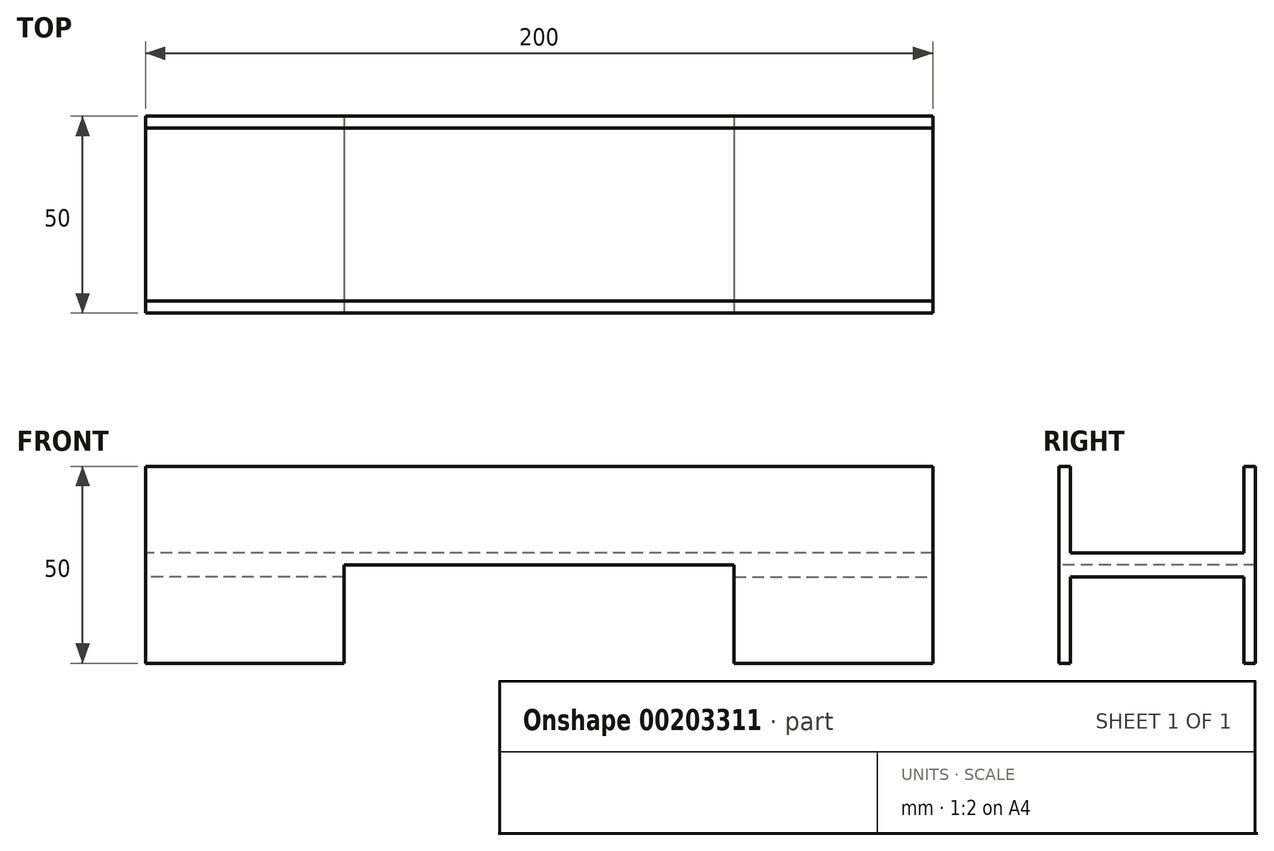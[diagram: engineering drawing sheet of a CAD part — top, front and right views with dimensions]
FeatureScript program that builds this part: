
annotation { "Feature Type Name" : "Feature", "Feature Type Description" : "" }
export const myFeature = defineFeature(function(context is Context, id is Id, definition is map)
    precondition{}
    {
        {
            var Q0;
            Q0=qCreatedBy(makeId("Front.planeOp"),FACE);
            var sketch = newSketch(context, id + "F0", { "sketchPlane" : qUnion([Q0])});
            skLineSegment(sketch, "E0.bottom", {"start": v(100, -12.5) * mm, "end": v(-100, -12.5) * mm});
            skLineSegment(sketch, "E0.top", {"start": v(100, 12.5) * mm, "end": v(-100, 12.5) * mm});
            skLineSegment(sketch, "E0.left", {"start": v(100, -12.5) * mm, "end": v(100, 12.5) * mm});
            skLineSegment(sketch, "E0.right", {"start": v(-100, -12.5) * mm, "end": v(-100, 12.5) * mm});
            skPoint(sketch, "E0.middle", {"position": v(0, 0) * mm});
            skSolve(sketch);
        }
        {
            var Q0;
            Q0 = qSketchRegion(id + "F0", true);
            extrude(context, id + "F1", {"entities" : qUnion([Q0]), "depth" : 50 * mm});
        }
        {
            var Q0;
            Q0=qCreatedBy(makeId("Right.planeOp"),FACE);
            var sketch = newSketch(context, id + "F2", { "sketchPlane" : qUnion([Q0])});
            skLineSegment(sketch, "E1.bottom", {"start": v(-47, 12.5) * mm, "end": v(-3, 12.5) * mm});
            skLineSegment(sketch, "E1.top", {"start": v(-47, -9.5) * mm, "end": v(-3, -9.5) * mm});
            skLineSegment(sketch, "E1.left", {"start": v(-47, 12.5) * mm, "end": v(-47, -9.5) * mm});
            skLineSegment(sketch, "E1.right", {"start": v(-3, 12.5) * mm, "end": v(-3, -9.5) * mm});
            skLineSegment(sketch, "E2", {"start": v(-50, 5.43) * mm, "end": v(-47, 5.43) * mm, "construction": true});
            skLineSegment(sketch, "E3", {"start": v(-21.48, -9.5) * mm, "end": v(-21.48, -12.5) * mm, "construction": true});
            skLineSegment(sketch, "E4", {"start": v(-3, 5.43) * mm, "end": v(0, 5.43) * mm, "construction": true});
            skSolve(sketch);
        }
        {
            var Q0;
            Q0 = qSketchRegion(id + "F2", true);
            extrude(context, id + "F3", {"entities" : qUnion([Q0]), "operationType" : NewBodyOperationType.REMOVE, "endBound" : BoundingType.THROUGH_ALL, "depth" : 25.4 * mm});
        }
        {
            var Q0;
            Q0 = qSketchRegion(id + "F2", true);
            extrude(context, id + "F4", {"entities" : qUnion([Q0]), "operationType" : NewBodyOperationType.REMOVE, "endBound" : BoundingType.THROUGH_ALL, "oppositeDirection" : true, "depth" : 25.4 * mm});
        }
        {
            var Q0;
            Q0=makeQuery(id+"F1.opExtrude","SWEPT_FACE",FACE,{"disambiguationData":[OSD([sQuery(id+"F0.wireOp",EDGE,"E0.bottom")])]});
            var sketch = newSketch(context, id + "F5", { "sketchPlane" : qUnion([Q0])});
            skLineSegment(sketch, "E5.bottom", {"start": v(100, 0) * mm, "end": v(49.53, 0) * mm});
            skLineSegment(sketch, "E5.top", {"start": v(100, 50) * mm, "end": v(49.53, 50) * mm});
            skLineSegment(sketch, "E5.left", {"start": v(100, 0) * mm, "end": v(100, 50) * mm});
            skLineSegment(sketch, "E5.right", {"start": v(49.53, 0) * mm, "end": v(49.53, 50) * mm});
            skSolve(sketch);
        }
        {
            var Q0;
            Q0=makeQuery(id+"F5.imprint","IMPRINT",FACE,{"disambiguationData":[TD([[makeQuery(id+"F5.imprint","IMPRINT",EDGE,{"derivedFrom":sQuery(id+"F5.wireOp",EDGE,"E5.bottom")}),-1.0]])]});
            extrude(context, id + "F6", {"entities" : qUnion([Q0]), "depth" : 25 * mm});
        }
        {
            var Q0;
            Q0=makeQuery(id+"F6.opExtrude","SWEPT_FACE",FACE,{"disambiguationData":[OSD([sQuery(id+"F5.wireOp",EDGE,"E5.left")])]});
            var sketch = newSketch(context, id + "F7", { "sketchPlane" : qUnion([Q0])});
            skLineSegment(sketch, "E6.bottom", {"start": v(-47, -37.5) * mm, "end": v(-3, -37.5) * mm});
            skLineSegment(sketch, "E6.top", {"start": v(-47, -15.5) * mm, "end": v(-3, -15.5) * mm});
            skLineSegment(sketch, "E6.left", {"start": v(-47, -37.5) * mm, "end": v(-47, -15.5) * mm});
            skLineSegment(sketch, "E6.right", {"start": v(-3, -37.5) * mm, "end": v(-3, -15.5) * mm});
            skLineSegment(sketch, "E7", {"start": v(-47, -31.95) * mm, "end": v(-50, -31.95) * mm});
            skLineSegment(sketch, "E8", {"start": v(-3, -31.95) * mm, "end": v(0, -31.95) * mm});
            skLineSegment(sketch, "E9", {"start": v(-24.8, -15.5) * mm, "end": v(-24.8, -12.5) * mm});
            skSolve(sketch);
        }
        {
            var Q0;
            Q0 = qSketchRegion(id + "F7", true);
            extrude(context, id + "F8", {"entities" : qUnion([Q0]), "operationType" : NewBodyOperationType.REMOVE, "endBound" : BoundingType.THROUGH_ALL, "oppositeDirection" : true, "depth" : 25.4 * mm});
        }
        {
            var Q0;
            Q0=makeQuery(id+"F6.opExtrude","SWEPT_BODY",BODY,{"disambiguationData":[OSD([sQuery(id+"F5.wireOp",EDGE,"E5.bottom"),sQuery(id+"F5.wireOp",EDGE,"E5.top"),sQuery(id+"F5.wireOp",EDGE,"E5.left"),sQuery(id+"F5.wireOp",EDGE,"E5.right")])]});
            var Q1;
            Q1=qCreatedBy(makeId("Right.planeOp"),FACE);
            mirror(context, id + "F9", {"operationType" : NewBodyOperationType.ADD, "entities" : qUnion([Q0]), "mirrorPlane" : qUnion([Q1])});
        }
    });
